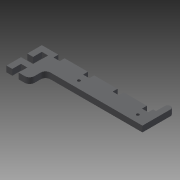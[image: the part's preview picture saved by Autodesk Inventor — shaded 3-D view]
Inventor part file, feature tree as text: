
AUTODESK INVENTOR PART (.ipt)
format: ipt  version: 2013 (Build 170138000, 138)  size: 122,368 bytes
history: native  units: mm
features: extrude x1, sketch x1
ambient origin geometry x8: Origin, YZ Plane, XZ Plane, XY Plane, X Axis, Y Axis, Z Axis, Center Point
bodies: Solid1 (feature_tree)
feature tree (2):
  extrude  "Extrusion1"  [1 undecoded]
  sketch  "Sketch1"  dims[d0=6.0mm d1=0.0mm]
note: 1 required parameter value undecoded (feature->parameter linkage not recoverable at this tier; creation-order binding heuristic only, values carry confidence <= 0.55)
